# Revit family: Toilet_Tissue_Holder-American_Standard-Studio_S-7105.230
name_source: partatom
category: Specialty Equipment
revit_build: Autodesk Revit 2018 (Build: 20170223_1515(x64)
units: mm (PartAtom-declared; Revit-internal decimal feet)

## family parameters
Cut with Voids When Loaded = No
Host = Face
OmniClass Number = 23.40.20.21.21
OmniClass Title = Toilet Paper Dispensers
Part Type = Normal
Room Calculation Point = No
Round Connector Dimension = Use Diameter
Shared = Yes

## types (3) — shared parameters
Assembly Code = C1030220
Default Elevation = 20"
Description = Studio S Toilet Paper Holder
Height = 2"
Installation Type = Wall Mounted
Length = 6 3/8"
Manufacturer = American Standard
Price = Prices may vary. Please consult Manufacturer Representative for most up-to-date price list.
Product Documentation Link = https://www.americanstandard-us.com
Product Page URL = https://www.americanstandard-us.com
Revised Date = 05/03/2021
Specification = Toilet Paper Holder shall feature metal construction. Shall feature concealed mounting with no exposed set screws. Toilet Paper Holder shall be American Standard Model 7105.230.
URL = https://www.americanstandard-us.com
Warranty Information = One Year General Product Warranty
Width = 4 1/16"

## per-type parameters (varying)
| type | Finish | Material |
| 7105.230.002 | Metal-American_Standard-002-Polished_Chrome | Metal-American_Standard-002-Polished_Chrome |
| 7105.230.243 | Metal-American_Standard-243-Matte_Black | Metal-American_Standard-243-Matte_Black |
| 7105.230.295 | Metal-American_Standard-295-Brushed_Nickel | Metal-American_Standard-295-Brushed_Nickel |

note: column(s) folded — value = type name in every type: Model

## geometry (parser evidence)
native form markers: Sweep x3
no freeform markers — native parametric forms only
